# Revit family: NBS_Allermuir_OffcChrs_Famiglia-en-us_HighBack
name_source: partatom
category: Furniture
revit_build: Autodesk Revit 2016 (Build: 20151007_0715(x64)
units: mm (PartAtom-declared; Revit-internal decimal feet)

## family parameters
Always vertical = Yes
Cut with Voids When Loaded = No
Room Calculation Point = No
Shared = No
Work Plane-Based = No

## types (4) — shared parameters
AssetType = Moveable
Category = Pr_40_50_12_57:Office chairs
CodePerformance = AMIS/BIFMA X5.1: 2011
DurationUnit = year
EnvironmentalProductDeclaration = http://www.thesenatorgroup.com
ExpectedLife = 10
FrameMountingMaterial = NBS_Concept
IfcExportAs = IfcFurnitureType
IfcExportType = CHAIR
IsBuiltIn = No
ManufacturerName = Allermuir
ManufacturerURL = http://www.thesenatorgroup.com
ModelReference = Famiglia high
NBSCertification = www.nationalbimlibrary.com/cert/hxdrqkke
NBSDescription = Office chairs
NBSReference = 45-35-20/330
OmniClassCode = 22-12 52 23
OmniClassTitle = Office Seating
OmniClassVersion = Table 22 2012-05-16
ProductInformation = http://www.thesenatorgroup.com
SeatBaseMaterial = NBS_Concept
SeatingSeatMaterial = NBS_Concept
SeatsAndBacksColourOptions = Black, White, Red, Light Grey, Dark Grey, Cream
SeatsAndBacksFinish = Fully upholstered
SeatsAndBacksFinishOptions = Decorative railroad stitch detail to perimeter seam, two-tone upholstery
StandardsDurability = ANSI/BIFMA X5.1: 2011
StandardsSafetyRequirements = ANSI/BIFMA X5.1: 2011
Status = UNSET
Uniclass2015Code = Pr_40_50_12_57
Uniclass2015Title = Office chairs
Uniclass2015Version = Products v1.9
Version = 1
WarrantyDescription = Allermuir warrant that its manufactured products are free from manufacturing defects in materials or workmanship for a period of ten years
WarrantyDurationParts = 10
WarrantyDurationUnit = year
WorkTableFrameMaterial = NBS_Concept
WorkTableMaterial = NBS_Concept

## per-type parameters (varying)
| type | Adjustability | BIMObjectName | Description | Features | FrameColour | FrameColourOptions | FrameFinish | FrameFinishOptions | FrameMaterials | HasWorkTable | HighestSeatingHeight | IntegralAccessories | LowestSeatingHeight | Name | NominalDepth | NominalHeight | NominalLength | NominalWidth | OfficeChairBase | SeatingHeight | SeatsAndBacksMaterial | Size |
| FMG302 |  | NBS_Allermuir_OfficeChairs_Famiglia_FMG302-US | High back on a 4 leg frame | Molded foam construction, fully upholstered, tubular steel frame with wire supports finished in polished chrome, plastic glides, tubular steel frame with wire supports available in slate grey powder coat | Chrome | Slate grey | Polished chrome | Available in slate grey powder coat | Tubular steel | No | 0 " | Plastic glides | 0 " | OfficeChairs_Famiglia_FMG302-US_Allermuir | 26 " | 49 " | 26 " | 26 " | NBS_Allermuir_OffcChrs_Famiglia_4LegFrameHigh | 18 " | Molded foam | 26 x 26 x 49.25" |
| FMG304 |  | NBS_Allermuir_OfficeChairs_Famiglia_FMG304-US | High back on a tilt frame | Molded foam construction, fully upholstered, tubular steel tilt frame finished in polished chrome | Chrome |  | Polished chrome | Available in slate grey powder coat | Tubular steel | No | 0 " |  | 0 " | OfficeChairs_Famiglia_FM304-US_Allermuir | 26 " | 45 " | 32 " | 26 " | NBS_Allermuir_OffcChrs_Famiglia_TiltFrame | 16 " | Molded foam | 26 x 45.25 x 32" |
| FMG306 | 16.75 - 21.75" | NBS_Allermuir_OfficeChairs_Famiglia_FMG306-US | High back on a 5 star base | Molded foam construction, fully upholstered, 5 star polished aluminum base, static yoke - swivel only, swivel column in anthracite, 2.5" hard wheel castors |  |  | Swivel column in anthracite, base polished aluminum |  | Aluminum | No | 22 " | 2.5" hard wheel castors | 17 " | OfficeChairs_Famiglia_FMG306-US_Allermuir | 26 " | 53 " | 26 " | 26 " | NBS_Allermuir_OffcChrs_Famiglia_5StarBase | 19 " | Molded foam | 25.5 x 52.5 x 25.5" |
| FMG307 |  | NBS_Allermuir_OfficeChairs_Famiglia_FMG307-US | High back on 5 star base with work surface | Molded foam construction, fully upholstered, 5 star polished aluminum base, static yoke - swivel only, swivel column in anthracite, soft touch PU orbital, fold down work surface in anthracite, 2.5" hard wheel castors |  |  | Swivel column in anthracite, base polished aluminum |  | Aluminum | Yes | 0 " | 2.5" hard wheel castors, soft touch pu orbital, fold down work surface in anthracite | 0 " | OfficeChairs_Famiglia_FMG307-US_Allermuir | 25 " | 49 " | 26 " | 25 " | NBS_Allermuir_OffcChrs_Famiglia_5StarBase | 19 " | Moulded foam | 24.5 x 26 x 49.5" |

note: column(s) folded — value = type name in every type: ModelNumber

## geometry (parser evidence)
native form markers: Sweep x15
no freeform markers — native parametric forms only
